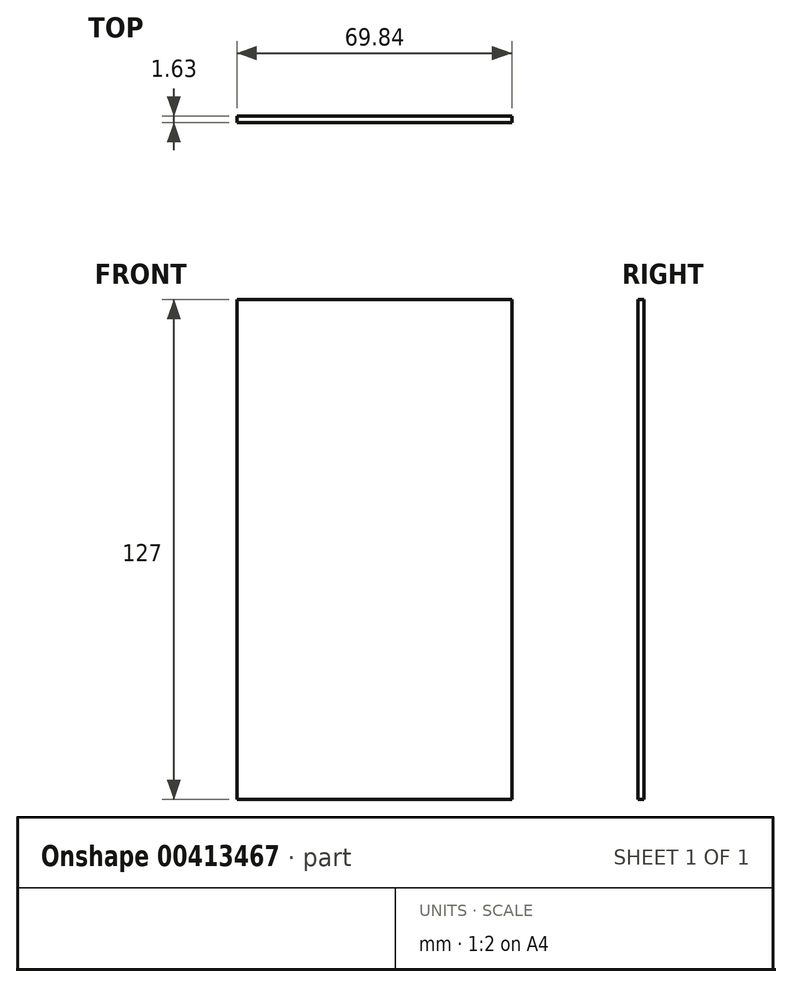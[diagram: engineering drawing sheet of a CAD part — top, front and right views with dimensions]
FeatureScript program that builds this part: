
annotation { "Feature Type Name" : "Feature", "Feature Type Description" : "" }
export const myFeature = defineFeature(function(context is Context, id is Id, definition is map)
    precondition{}
    {
        {
            var Q0;
            Q0=qCreatedBy(makeId("Front.planeOp"),FACE);
            var sketch = newSketch(context, id + "F0", { "sketchPlane" : qUnion([Q0])});
            skLineSegment(sketch, "E0.bottom", {"start": v(34.92, 63.5) * mm, "end": v(-34.93, 63.5) * mm});
            skLineSegment(sketch, "E0.top", {"start": v(34.93, -63.5) * mm, "end": v(-34.92, -63.5) * mm});
            skLineSegment(sketch, "E0.left", {"start": v(34.92, 63.5) * mm, "end": v(34.93, -63.5) * mm});
            skLineSegment(sketch, "E0.right", {"start": v(-34.93, 63.5) * mm, "end": v(-34.93, -63.5) * mm});
            skPoint(sketch, "E0.middle", {"position": v(0, 0) * mm});
            skSolve(sketch);
        }
        {
            var Q0;
            Q0=makeQuery(id+"F0.imprint","IMPRINT",FACE,{"disambiguationData":[TD([[makeQuery(id+"F0.imprint","IMPRINT",EDGE,{"derivedFrom":sQuery(id+"F0.wireOp",EDGE,"E0.bottom")}),1.0]])]});
            extrude(context, id + "F1", {"entities" : qUnion([Q0]), "depth" : 1.63 * mm});
        }
    });
